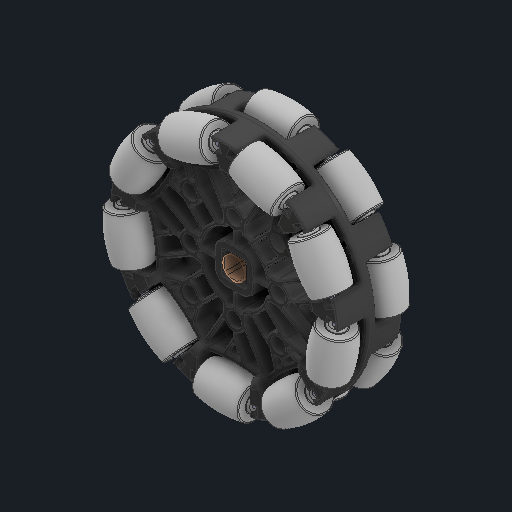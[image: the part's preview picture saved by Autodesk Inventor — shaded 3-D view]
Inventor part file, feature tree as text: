
AUTODESK INVENTOR PART (.ipt)
format: ipt  version: 2025 (Build 290162000, 162)  size: 28,569,088 bytes
history: native  units: in
note: dims shown in document units (in); Inventor stores cm internally (conversion verified against a paired STEP export)
features: other x59, sketch x1
ambient origin geometry x8: Origin, YZ Plane, XZ Plane, XY Plane, X Axis, Y Axis, Z Axis, Center Point
bodies: Solid1 (feature_tree), Solid2 (feature_tree), Solid3 (feature_tree), Solid4 (feature_tree), Solid5 (feature_tree), Solid6 (feature_tree), Solid7 (feature_tree), Solid8 (feature_tree), Solid9 (feature_tree), Solid10 (feature_tree), Solid11 (feature_tree), Solid12 (feature_tree), Solid13 (feature_tree), Solid14 (feature_tree), Solid15 (feature_tree), Solid16 (feature_tree), Solid17 (feature_tree), Solid18 (feature_tree), Solid19 (feature_tree), Solid20 (feature_tree), Solid21 (feature_tree), Solid22 (feature_tree), Solid23 (feature_tree), Solid24 (feature_tree), Solid25 (feature_tree), Solid26 (feature_tree), Solid27 (feature_tree), Solid28 (feature_tree), Solid29 (feature_tree), Solid30 (feature_tree), Solid31 (feature_tree), Solid32 (feature_tree), Solid33 (feature_tree), Solid34 (feature_tree), Solid35 (feature_tree), Solid36 (feature_tree), Solid37 (feature_tree), Solid38 (feature_tree), Solid39 (feature_tree), Solid40 (feature_tree), Solid41 (feature_tree), Solid42 (feature_tree), Solid43 (feature_tree), Solid44 (feature_tree), Solid45 (feature_tree), Solid46 (feature_tree), Solid47 (feature_tree), Solid48 (feature_tree), Solid49 (feature_tree), Solid50 (feature_tree), Solid51 (feature_tree), Solid52 (feature_tree), Solid53 (feature_tree), Solid54 (feature_tree), Solid55 (feature_tree)
feature tree (60):
  other  "2.75 Omni Antistatic.ipt"
  other  "Solid1::2.75 Omni Antistatic.ipt"
  other  "Solid2::2.75 Omni Antistatic.ipt"
  other  "Solid3::2.75 Omni Antistatic.ipt"
  other  "Solid4::2.75 Omni Antistatic.ipt"
  other  "Solid5::2.75 Omni Antistatic.ipt"
  other  "Solid6::2.75 Omni Antistatic.ipt"
  other  "Solid7::2.75 Omni Antistatic.ipt"
  other  "Solid8::2.75 Omni Antistatic.ipt"
  other  "Solid9::2.75 Omni Antistatic.ipt"
  other  "Solid10::2.75 Omni Antistatic.ipt"
  other  "Solid11::2.75 Omni Antistatic.ipt"
  other  "Solid12::2.75 Omni Antistatic.ipt"
  other  "Solid13::2.75 Omni Antistatic.ipt"
  other  "Solid14::2.75 Omni Antistatic.ipt"
  other  "Solid15::2.75 Omni Antistatic.ipt"
  other  "Solid16::2.75 Omni Antistatic.ipt"
  other  "Solid17::2.75 Omni Antistatic.ipt"
  other  "Solid18::2.75 Omni Antistatic.ipt"
  other  "Solid19::2.75 Omni Antistatic.ipt"
  other  "Solid20::2.75 Omni Antistatic.ipt"
  other  "Solid21::2.75 Omni Antistatic.ipt"
  other  "Solid22::2.75 Omni Antistatic.ipt"
  other  "Solid23::2.75 Omni Antistatic.ipt"
  other  "Solid24::2.75 Omni Antistatic.ipt"
  other  "Solid25::2.75 Omni Antistatic.ipt"
  other  "Solid26::2.75 Omni Antistatic.ipt"
  other  "Solid27::2.75 Omni Antistatic.ipt"
  other  "Solid28::2.75 Omni Antistatic.ipt"
  other  "Solid29::2.75 Omni Antistatic.ipt"
  other  "Solid30::2.75 Omni Antistatic.ipt"
  other  "Solid31::2.75 Omni Antistatic.ipt"
  other  "Solid32::2.75 Omni Antistatic.ipt"
  other  "Solid33::2.75 Omni Antistatic.ipt"
  other  "Solid34::2.75 Omni Antistatic.ipt"
  other  "Solid35::2.75 Omni Antistatic.ipt"
  other  "Solid36::2.75 Omni Antistatic.ipt"
  other  "Solid37::2.75 Omni Antistatic.ipt"
  other  "Solid38::2.75 Omni Antistatic.ipt"
  other  "Solid39::2.75 Omni Antistatic.ipt"
  other  "Solid40::2.75 Omni Antistatic.ipt"
  other  "Solid41::2.75 Omni Antistatic.ipt"
  other  "Solid42::2.75 Omni Antistatic.ipt"
  other  "Solid43::2.75 Omni Antistatic.ipt"
  other  "Solid44::2.75 Omni Antistatic.ipt"
  other  "Solid45::2.75 Omni Antistatic.ipt"
  other  "Solid46::2.75 Omni Antistatic.ipt"
  other  "Solid47::2.75 Omni Antistatic.ipt"
  other  "Solid48::2.75 Omni Antistatic.ipt"
  other  "Solid49::2.75 Omni Antistatic.ipt"
  other  "Solid50::2.75 Omni Antistatic.ipt"
  other  "Solid51::2.75 Omni Antistatic.ipt"
  other  "Solid52::2.75 Omni Antistatic.ipt"
  other  "Solid53::2.75 Omni Antistatic.ipt"
  other  "Solid54::2.75 Omni Antistatic.ipt"
  other  "Solid55::2.75 Omni Antistatic.ipt"
  other  "TaggingFeature1"
  sketch  "Sketch1"  dims[d0=0.3937in]
  other  "Srf1"
  other  "Srf1::Derived"
